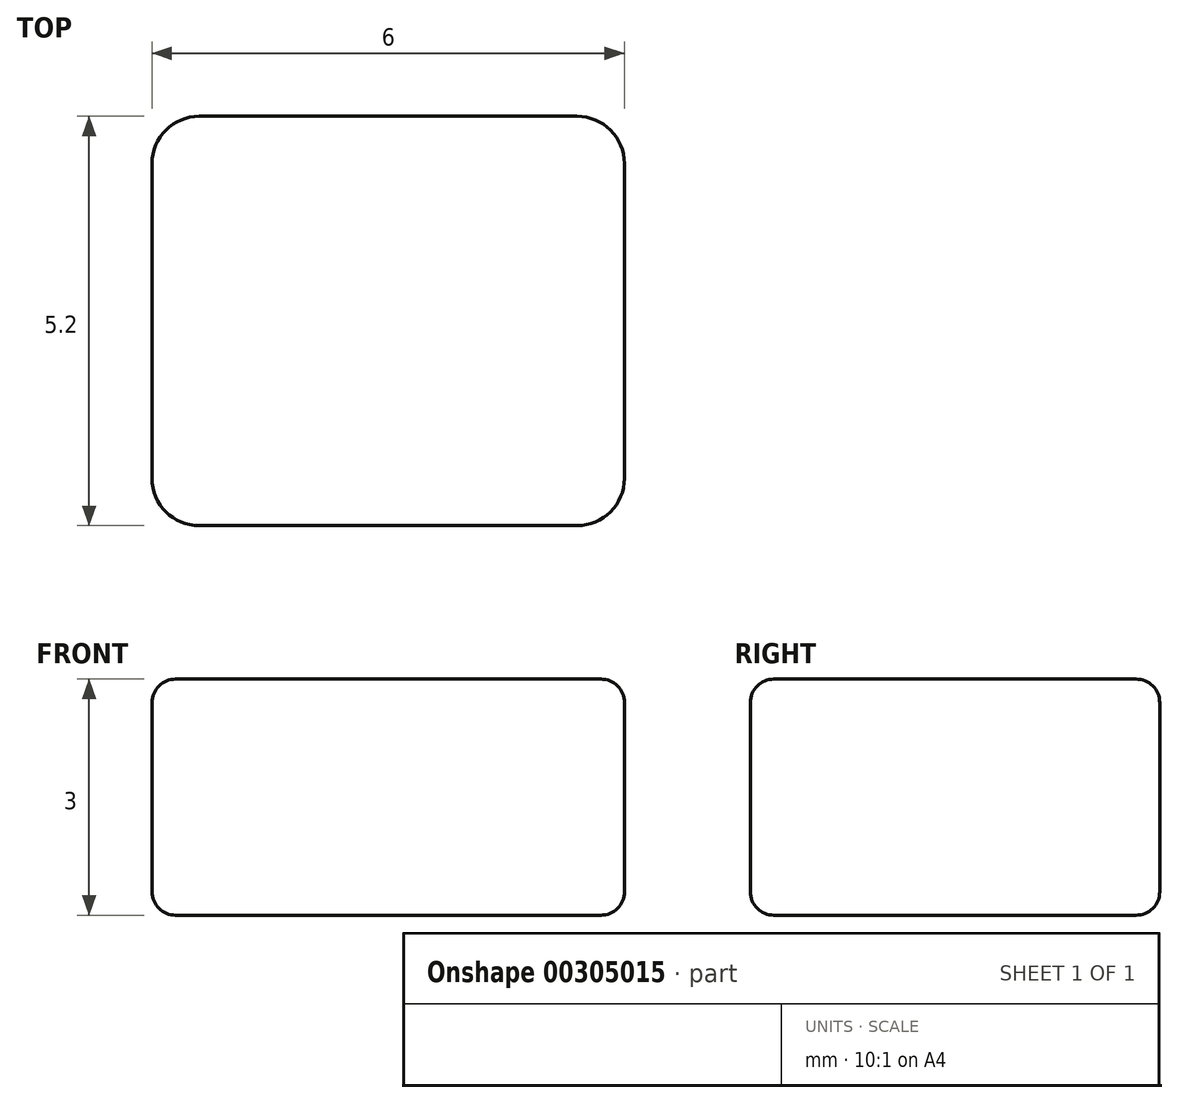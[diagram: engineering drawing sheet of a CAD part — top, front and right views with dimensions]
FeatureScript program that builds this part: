
annotation { "Feature Type Name" : "Feature", "Feature Type Description" : "" }
export const myFeature = defineFeature(function(context is Context, id is Id, definition is map)
    precondition{}
    {
        {
            var Q0;
            Q0=qCreatedBy(makeId("Top.planeOp"),FACE);
            var sketch = newSketch(context, id + "F0", { "sketchPlane" : qUnion([Q0])});
            skLineSegment(sketch, "E0.bottom", {"start": v(0, 0) * mm, "end": v(6, 0) * mm});
            skLineSegment(sketch, "E0.top", {"start": v(0, 5.2) * mm, "end": v(6, 5.2) * mm});
            skLineSegment(sketch, "E0.left", {"start": v(0, 0) * mm, "end": v(0, 5.2) * mm});
            skLineSegment(sketch, "E0.right", {"start": v(6, 0) * mm, "end": v(6, 5.2) * mm});
            skSolve(sketch);
        }
        {
            var Q0;
            Q0 = qSketchRegion(id + "F0", true);
            extrude(context, id + "F1", {"entities" : qUnion([Q0]), "depth" : 3 * mm});
        }
        {
            var Q0;
            Q0=makeQuery(id+"F1.opExtrude","SWEPT_EDGE",EDGE,{"disambiguationData":[OSD([sQuery(id+"F0.wireOp",EDGE,"E0.top"),sQuery(id+"F0.wireOp",EDGE,"E0.right")])]});
            var Q1;
            Q1=makeQuery(id+"F1.opExtrude","SWEPT_EDGE",EDGE,{"disambiguationData":[OSD([sQuery(id+"F0.wireOp",EDGE,"E0.bottom"),sQuery(id+"F0.wireOp",EDGE,"E0.right")])]});
            var Q2;
            Q2=makeQuery(id+"F1.opExtrude","SWEPT_EDGE",EDGE,{"disambiguationData":[OSD([sQuery(id+"F0.wireOp",EDGE,"E0.bottom"),sQuery(id+"F0.wireOp",EDGE,"E0.left")])]});
            var Q3;
            Q3=makeQuery(id+"F1.opExtrude","SWEPT_EDGE",EDGE,{"disambiguationData":[OSD([sQuery(id+"F0.wireOp",EDGE,"E0.top"),sQuery(id+"F0.wireOp",EDGE,"E0.left")])]});
            fillet(context, id + "F2", {"entities" : qUnion([Q0, Q1, Q2, Q3]), "radius" : 0.6 * mm, "tangentPropagation" : true, "allowEdgeOverflow" : false});
        }
        {
            var Q0;
            Q0=makeQuery(id+"F1.opExtrude","CAP_FACE",FACE,{"disambiguationData":[OSD([sQuery(id+"F0.wireOp",EDGE,"E0.bottom"),sQuery(id+"F0.wireOp",EDGE,"E0.top"),sQuery(id+"F0.wireOp",EDGE,"E0.left"),sQuery(id+"F0.wireOp",EDGE,"E0.right")])],"isStart":false});
            var Q1;
            Q1=makeQuery(id+"F1.opExtrude","CAP_FACE",FACE,{"disambiguationData":[OSD([sQuery(id+"F0.wireOp",EDGE,"E0.bottom"),sQuery(id+"F0.wireOp",EDGE,"E0.top"),sQuery(id+"F0.wireOp",EDGE,"E0.left"),sQuery(id+"F0.wireOp",EDGE,"E0.right")])],"isStart":true});
            fillet(context, id + "F3", {"entities" : qUnion([Q0, Q1]), "radius" : 0.3 * mm, "tangentPropagation" : true, "allowEdgeOverflow" : false});
        }
    });
